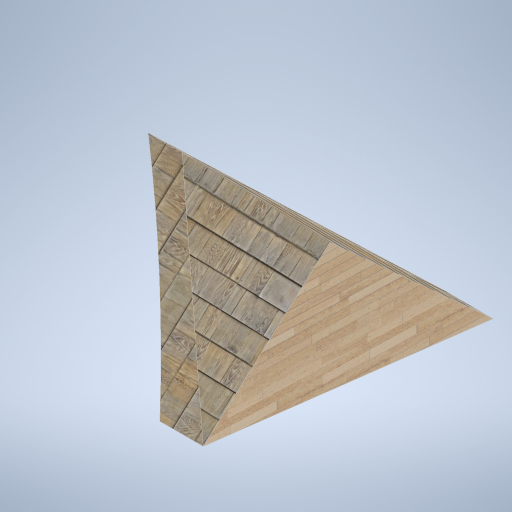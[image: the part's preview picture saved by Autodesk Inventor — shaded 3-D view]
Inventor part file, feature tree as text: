
AUTODESK INVENTOR PART (.ipt)
format: ipt  version: 2024.2 (Build 282272000, 272)  size: 453,120 bytes
history: native  units: in
note: dims shown in document units (in); Inventor stores cm internally (conversion verified against a paired STEP export)
features: sketch x7, plane x6, other x3
ambient origin geometry x8: Origin, YZ Plane, XZ Plane, XY Plane, X Axis, Y Axis, Z Axis, Center Point
bodies: Solid1 (feature_tree)
feature tree (16):
  other  "panel_pad_02 .ipt"
  other  "Solid1::panel_pad_02 .ipt"
  other  "TaggingFeature1"
  sketch  "Sketch1"  dims[d0=0.3937in]
  sketch  "Sketch2"
  sketch  "Sketch3"
  sketch  "Sketch6"
  sketch  "Sketch7"
  sketch  "Sketch8"
  sketch  "Sketch9"
  plane  "Work Plane1"
  plane  "Work Plane2"
  plane  "Work Plane3"
  plane  "Work Plane4"
  plane  "Work Plane5"
  plane  "Work Plane6"
